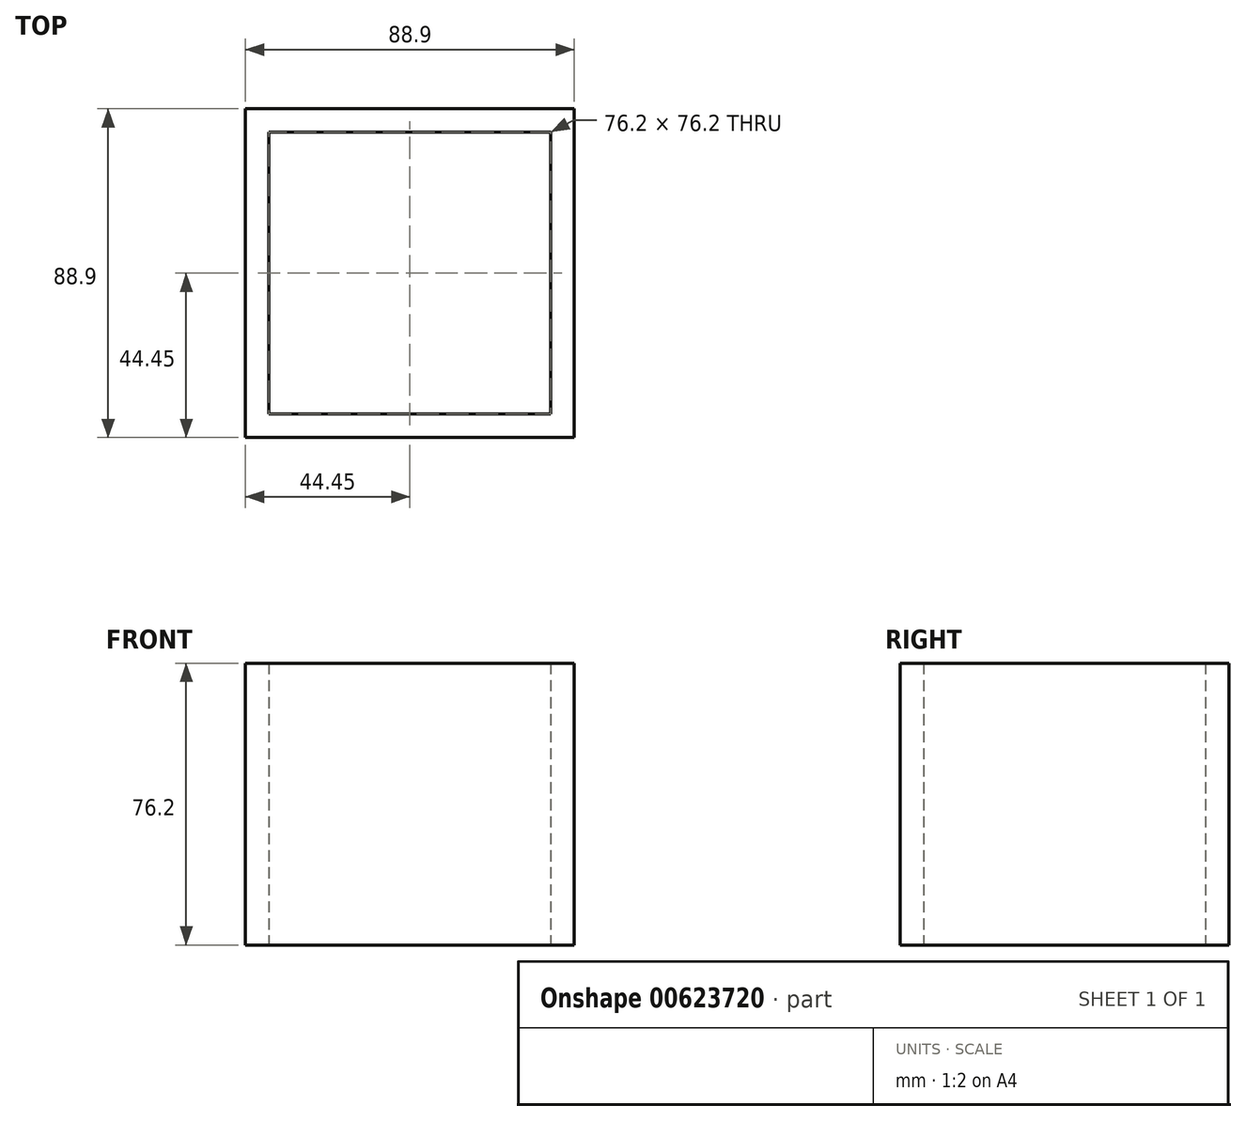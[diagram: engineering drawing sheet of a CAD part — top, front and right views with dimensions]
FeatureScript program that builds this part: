
annotation { "Feature Type Name" : "Feature", "Feature Type Description" : "" }
export const myFeature = defineFeature(function(context is Context, id is Id, definition is map)
    precondition{}
    {
        {
            var Q0;
            Q0=qCreatedBy(makeId("Top.planeOp"),FACE);
            var sketch = newSketch(context, id + "F0", { "sketchPlane" : qUnion([Q0])});
            skLineSegment(sketch, "E0.bottom", {"start": v(38.1, 38.1) * mm, "end": v(-38.1, 38.1) * mm});
            skLineSegment(sketch, "E0.top", {"start": v(38.1, -38.1) * mm, "end": v(-38.1, -38.1) * mm});
            skLineSegment(sketch, "E0.left", {"start": v(38.1, 38.1) * mm, "end": v(38.1, -38.1) * mm});
            skLineSegment(sketch, "E0.right", {"start": v(-38.1, 38.1) * mm, "end": v(-38.1, -38.1) * mm});
            skPoint(sketch, "E0.middle", {"position": v(0, 0) * mm});
            skLineSegment(sketch, "E1.bottom", {"start": v(44.45, 44.45) * mm, "end": v(-44.45, 44.45) * mm});
            skLineSegment(sketch, "E1.top", {"start": v(44.45, -44.45) * mm, "end": v(-44.45, -44.45) * mm});
            skLineSegment(sketch, "E1.left", {"start": v(44.45, 44.45) * mm, "end": v(44.45, -44.45) * mm});
            skLineSegment(sketch, "E1.right", {"start": v(-44.45, 44.45) * mm, "end": v(-44.45, -44.45) * mm});
            skSolve(sketch);
        }
        {
            var Q0;
            Q0 = qSketchRegion(id + "F0", true);
            extrude(context, id + "F1", {"entities" : qUnion([Q0]), "depth" : 76.2 * mm, "offsetDistance" : 25.4 * mm});
        }
    });
